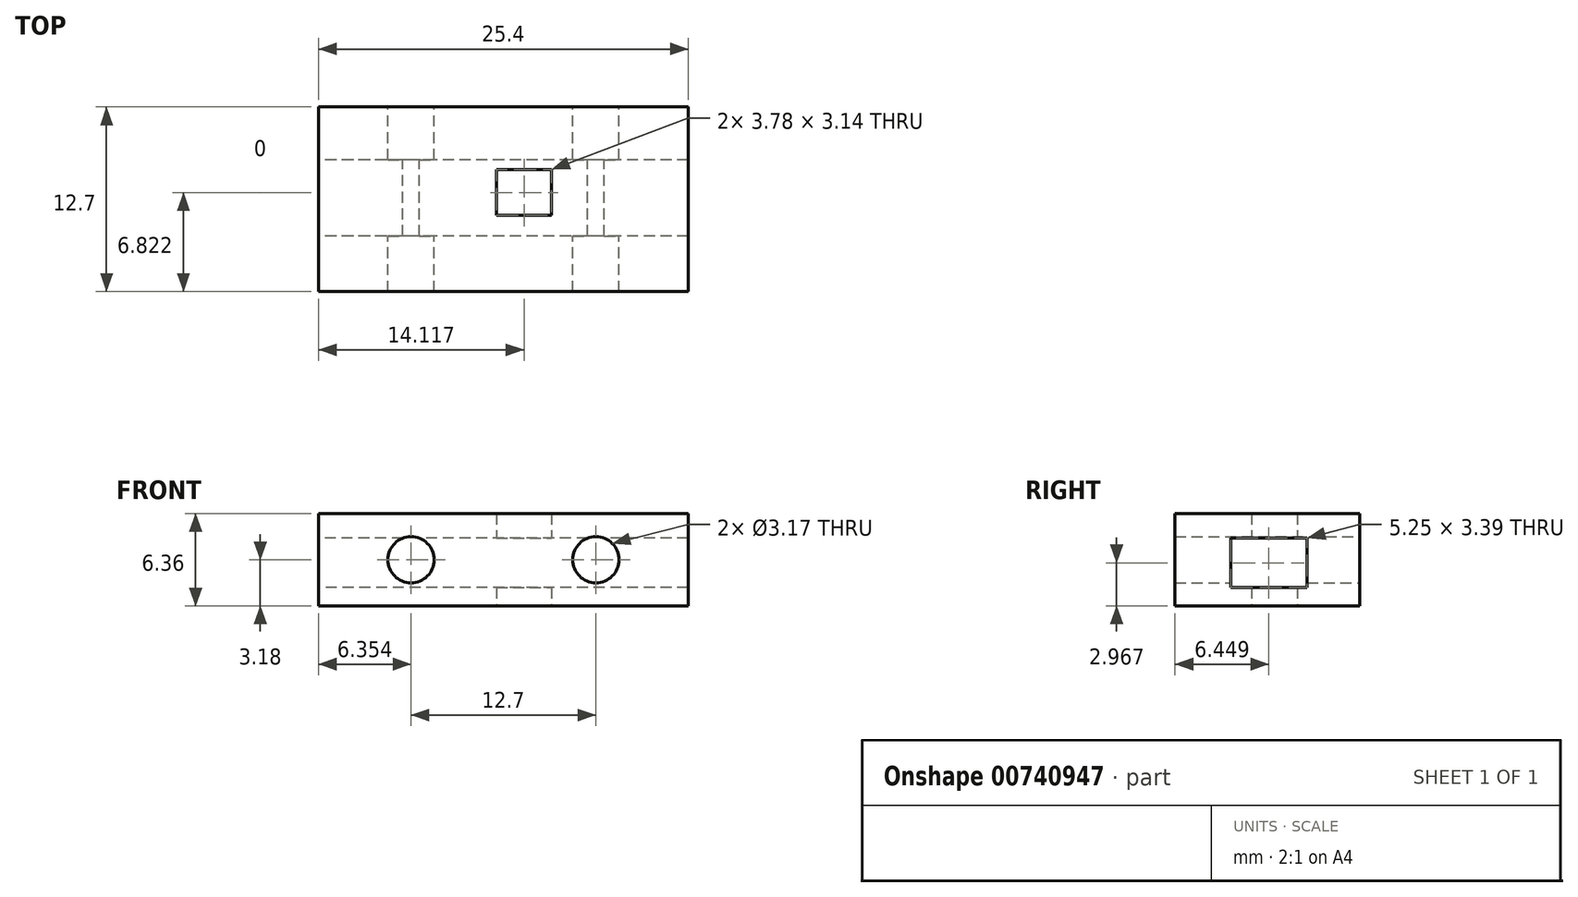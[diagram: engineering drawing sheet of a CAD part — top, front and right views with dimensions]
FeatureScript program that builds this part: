
annotation { "Feature Type Name" : "Feature", "Feature Type Description" : "" }
export const myFeature = defineFeature(function(context is Context, id is Id, definition is map)
    precondition{}
    {
        {
            var Q0;
            Q0=qCreatedBy(makeId("Front.planeOp"),FACE);
            var sketch = newSketch(context, id + "F0", { "sketchPlane" : qUnion([Q0])});
            skLineSegment(sketch, "E0.bottom", {"start": v(-7.94, 3.18) * mm, "end": v(17.46, 3.18) * mm});
            skLineSegment(sketch, "E0.top", {"start": v(-7.94, -3.18) * mm, "end": v(17.46, -3.18) * mm});
            skLineSegment(sketch, "E0.left", {"start": v(-7.94, 3.18) * mm, "end": v(-7.94, -3.18) * mm});
            skLineSegment(sketch, "E0.right", {"start": v(17.46, 3.18) * mm, "end": v(17.46, -3.18) * mm});
            skCircle(sketch, "E1", {"center": v(-1.59, 0) * mm, "radius": 1.59 * mm});
            skCircle(sketch, "E2", {"center": v(11.11, 0) * mm, "radius": 1.59 * mm});
            skSolve(sketch);
        }
        {
            var Q0;
            Q0=makeQuery(id+"F0.imprint","IMPRINT",FACE,{"disambiguationData":[TD([[makeQuery(id+"F0.imprint","IMPRINT",EDGE,{"derivedFrom":sQuery(id+"F0.wireOp",EDGE,"E0.bottom")}),-1.0]])]});
            extrude(context, id + "F1", {"entities" : qUnion([Q0]), "depth" : 12.7 * mm, "offsetDistance" : 25.4 * mm});
        }
        {
            var Q0;
            Q0=makeQuery(id+"F1.opExtrude","SWEPT_FACE",FACE,{"disambiguationData":[OSD([sQuery(id+"F0.wireOp",EDGE,"E0.top")])]});
            var sketch = newSketch(context, id + "F2", { "sketchPlane" : qUnion([Q0])});
            skLineSegment(sketch, "E3.bottom", {"start": v(8.07, 4.3) * mm, "end": v(4.28, 4.3) * mm});
            skLineSegment(sketch, "E3.top", {"start": v(8.07, 7.45) * mm, "end": v(4.28, 7.45) * mm});
            skLineSegment(sketch, "E3.left", {"start": v(8.07, 4.3) * mm, "end": v(8.07, 7.45) * mm});
            skLineSegment(sketch, "E3.right", {"start": v(4.28, 4.3) * mm, "end": v(4.28, 7.45) * mm});
            skSolve(sketch);
        }
        {
            var Q0;
            Q0 = qSketchRegion(id + "F2", true);
            extrude(context, id + "F3", {"entities" : qUnion([Q0]), "operationType" : NewBodyOperationType.REMOVE, "oppositeDirection" : true, "depth" : 25.4 * mm, "offsetDistance" : 25.4 * mm});
        }
        {
            var Q0;
            Q0=makeQuery(id+"F1.opExtrude","SWEPT_FACE",FACE,{"disambiguationData":[OSD([sQuery(id+"F0.wireOp",EDGE,"E0.left")])]});
            var sketch = newSketch(context, id + "F4", { "sketchPlane" : qUnion([Q0])});
            skLineSegment(sketch, "E4.bottom", {"start": v(3.63, 1.48) * mm, "end": v(8.87, 1.48) * mm});
            skLineSegment(sketch, "E4.top", {"start": v(3.63, -1.9) * mm, "end": v(8.87, -1.9) * mm});
            skLineSegment(sketch, "E4.left", {"start": v(3.63, 1.48) * mm, "end": v(3.63, -1.9) * mm});
            skLineSegment(sketch, "E4.right", {"start": v(8.87, 1.48) * mm, "end": v(8.87, -1.9) * mm});
            skSolve(sketch);
        }
        {
            var Q0;
            Q0=makeQuery(id+"F4.imprint","IMPRINT",FACE,{"disambiguationData":[TD([[makeQuery(id+"F4.imprint","IMPRINT",EDGE,{"derivedFrom":sQuery(id+"F4.wireOp",EDGE,"E4.bottom")}),-1.0]])]});
            extrude(context, id + "F5", {"entities" : qUnion([Q0]), "operationType" : NewBodyOperationType.REMOVE, "oppositeDirection" : true, "depth" : 25.4 * mm, "offsetDistance" : 25.4 * mm});
        }
        {
            var Q0;
            Q0=makeQuery(id+"F0.imprint","IMPRINT",FACE,{"disambiguationData":[TD([[makeQuery(id+"F0.imprint","IMPRINT",EDGE,{"derivedFrom":sQuery(id+"F0.wireOp",EDGE,"E0.bottom")}),-1.0]])]});
            var sketch = newSketch(context, id + "F6", { "sketchPlane" : qUnion([Q0])});
            skCircle(sketch, "E5", {"center": v(5.72, 0) * mm, "radius": 2.11 * mm});
            skSolve(sketch);
        }
        {
            var Q0;
            Q0=makeQuery(id+"F6.imprint","IMPRINT",FACE,{"disambiguationData":[TD([[makeQuery(id+"F6.imprint","IMPRINT",EDGE,{"derivedFrom":sQuery(id+"F6.wireOp",EDGE,"E5")}),1.0]])]});
            var Q1;
            Q1=sQuery(id+"F6.wireOp",EDGE,"E5");
            extrude(context, id + "F7", {"entities" : qUnion([Q0]), "operationType" : NewBodyOperationType.REMOVE, "surfaceEntities" : qUnion([Q1]), "oppositeDirection" : true, "depth" : 25.4 * mm, "offsetDistance" : 25.4 * mm});
        }
    });
